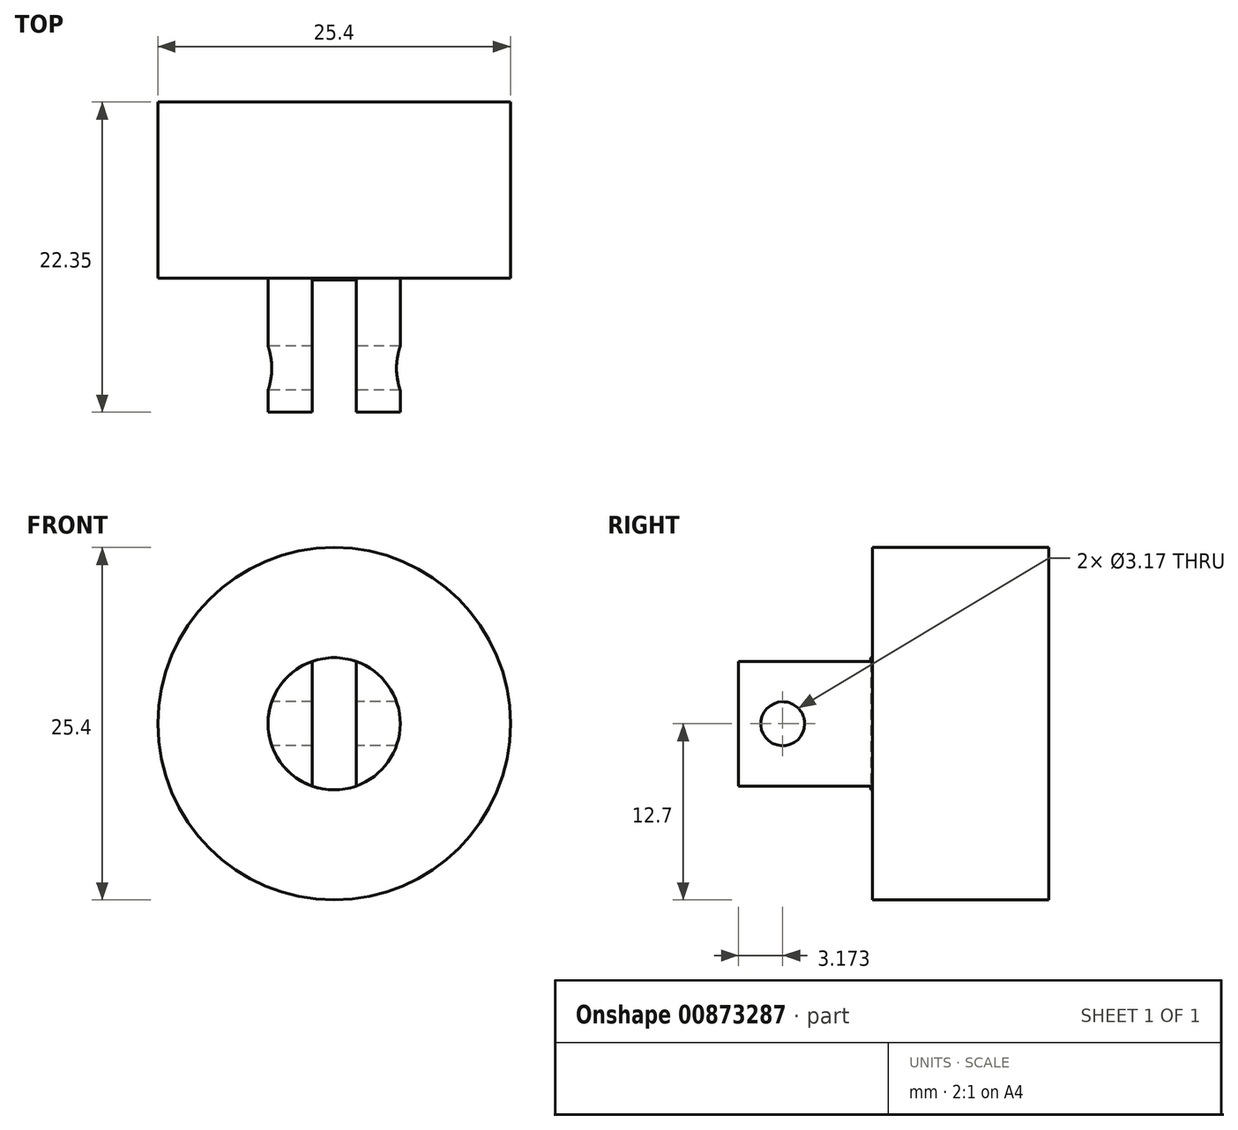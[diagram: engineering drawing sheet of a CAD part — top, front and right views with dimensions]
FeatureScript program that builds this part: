
annotation { "Feature Type Name" : "Feature", "Feature Type Description" : "" }
export const myFeature = defineFeature(function(context is Context, id is Id, definition is map)
    precondition{}
    {
        {
            var Q0;
            Q0=qCreatedBy(makeId("Front.planeOp"),FACE);
            var sketch = newSketch(context, id + "F0", { "sketchPlane" : qUnion([Q0])});
            skCircle(sketch, "E0", {"center": v(0, 0) * mm, "radius": 12.7 * mm});
            skSolve(sketch);
        }
        {
            var Q0;
            Q0=makeQuery(id+"F0.imprint","IMPRINT",FACE,{"disambiguationData":[TD([[makeQuery(id+"F0.imprint","IMPRINT",EDGE,{"derivedFrom":sQuery(id+"F0.wireOp",EDGE,"E0")}),1.0]])]});
            extrude(context, id + "F1", {"entities" : qUnion([Q0]), "depth" : 12.7 * mm, "offsetDistance" : 25.4 * mm});
        }
        {
            var Q0;
            Q0=makeQuery(id+"F1.opExtrude","CAP_FACE",FACE,{"disambiguationData":[OSD([sQuery(id+"F0.wireOp",EDGE,"E0")])],"isStart":false});
            var sketch = newSketch(context, id + "F2", { "sketchPlane" : qUnion([Q0])});
            skCircle(sketch, "E1", {"center": v(0, 0) * mm, "radius": 4.76 * mm});
            skSolve(sketch);
        }
        {
            var Q0;
            Q0=makeQuery(id+"F2.imprint","IMPRINT",FACE,{"disambiguationData":[TD([[makeQuery(id+"F2.imprint","IMPRINT",EDGE,{"derivedFrom":sQuery(id+"F2.wireOp",EDGE,"E1")}),1.0]])]});
            extrude(context, id + "F3", {"entities" : qUnion([Q0]), "operationType" : NewBodyOperationType.ADD, "depth" : 9.65 * mm, "offsetDistance" : 25.4 * mm});
        }
        {
            var Q0;
            Q0=makeQuery(id+"F3.opExtrude","CAP_FACE",FACE,{"disambiguationData":[OSD([sQuery(id+"F2.wireOp",EDGE,"E1")])],"isStart":false});
            var sketch = newSketch(context, id + "F4", { "sketchPlane" : qUnion([Q0])});
            skLineSegment(sketch, "E2", {"start": v(-1.59, 5.16) * mm, "end": v(-1.59, -5.77) * mm});
            skLineSegment(sketch, "E3", {"start": v(1.59, 5.25) * mm, "end": v(1.59, -6) * mm});
            skSolve(sketch);
        }
        {
            var Q0;
            {var subQ0=sQuery(id+"F4.wireOp",EDGE,"E2");var subQ1=makeQuery(id+"F3.opExtrude","CAP_EDGE",EDGE,{"disambiguationData":[OSD([sQuery(id+"F2.wireOp",EDGE,"E1")])],"isStart":false});var subQ2=makeQuery(id+"F4.imprint","INTERSECT",VERTEX,{"disambiguationData":[OD(0.0)],"derivedFrom":[subQ1,subQ0]});Q0=makeQuery(id+"F4.imprint","IMPRINT",FACE,{"disambiguationData":[TD([[makeQuery(id+"F4.imprint","IMPRINT",EDGE,{"disambiguationData":[TD([[subQ2,1.0]])],"derivedFrom":subQ0}),1.0]])]});}
            extrude(context, id + "F5", {"entities" : qUnion([Q0]), "operationType" : NewBodyOperationType.REMOVE, "oppositeDirection" : true, "depth" : 9.52 * mm, "offsetDistance" : 25.4 * mm});
        }
        {
            var Q0;
            Q0=makeQuery(id+"F5.boolean.opBoolean","COPY",FACE,{"derivedFrom":makeQuery(id+"F5.opExtrude","SWEPT_FACE",FACE,{"disambiguationData":[OSD([sQuery(id+"F4.wireOp",EDGE,"E2")])]})});
            var sketch = newSketch(context, id + "F6", { "sketchPlane" : qUnion([Q0])});
            skCircle(sketch, "E4", {"center": v(-19.18, 0) * mm, "radius": 1.59 * mm});
            skPoint(sketch, "E4.centerSnap0", {"position": v(-22.35, 0) * mm});
            skSolve(sketch);
        }
        {
            var Q0;
            Q0=makeQuery(id+"F6.imprint","IMPRINT",FACE,{"disambiguationData":[TD([[makeQuery(id+"F6.imprint","IMPRINT",EDGE,{"derivedFrom":sQuery(id+"F6.wireOp",EDGE,"E4")}),1.0]])]});
            extrude(context, id + "F7", {"entities" : qUnion([Q0]), "operationType" : NewBodyOperationType.REMOVE, "endBound" : BoundingType.SYMMETRIC, "depth" : 12.7 * mm, "offsetDistance" : 25.4 * mm});
        }
    });
